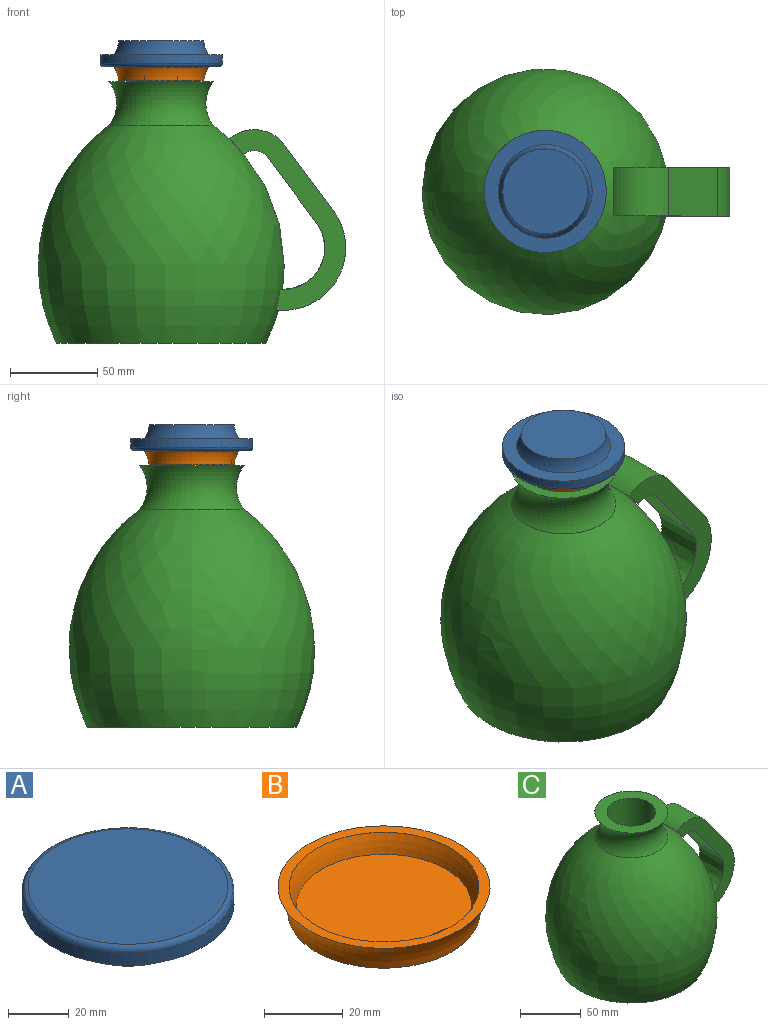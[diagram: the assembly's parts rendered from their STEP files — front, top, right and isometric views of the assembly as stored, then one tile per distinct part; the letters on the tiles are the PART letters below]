
ASSEMBLY  parts=3 mates=2
PART A: 6 faces, bbox 75.8x75.8x17 mm
  f0: plane 48.64x48.64mm, normal (0,0,-1), area 1858.2mm2, adj f1
  f1: torus R=44.22mm, axis (0,0,-1), area 1347.6mm2, adj f0,f2
  f2: plane 70x70mm, normal (0,0,-1), area 1575.2mm2, adj f1,f3
  f3: cylinder r=35mm len=70mm, axis (0,0,-1), area 1099.6mm2, adj f2,f5
  f4: plane 66x66mm, normal (0,0,1), area 3421.2mm2, adj f5
  f5: torus R=33mm, axis (0,0,1), area 676.5mm2, adj f3,f4
PART B: 7 faces, bbox 65.2x65.2x16 mm
  f0: cylinder r=12mm len=18.8mm, axis (0,0,-1), area 69.7mm2, adj f1,f3,f4,f5,f6
  f1: plane 48.84x46.96mm, normal (0,0,-1), area 1790.3mm2, adj f0,f2
  f2: torus R=44.32mm, axis (0,0,-1), area 1353mm2, adj f1,f3,f4
  f3: plane 54x54mm, normal (0,0,1), area 450.8mm2, adj f0,f2,f4,f6
  f4: cylinder r=24.42mm len=18.8mm, axis (0,0,-1), area 154.4mm2, adj f0,f2,f3
  f5: plane 44.55x43.14mm, normal (0,0,1), area 1513.5mm2, adj f0,f6
  f6: torus R=44.32mm, axis (0,0,-1), area 745.5mm2, adj f0,f3,f5
PART C: 16 faces, bbox 176.4x141.1x151.8 mm
  f0: plane 120x120mm, normal (0,0,-1), area 11309.7mm2, adj f1
  f1: revolved ~140.99x140.99mm, area 52192.3mm2, adj f0,f2,f4,f8,f10,f11,f12,f13
  f2: torus R=45.61mm, axis (0,0,-1), area 4597.9mm2, adj f1,f3
  f3: plane 60x60mm, normal (0,0,1), area 1570.8mm2, adj f2,f14
  f4: plane 28x9.21mm, normal (-0.77,0,-0.64), area 210.6mm2, adj f1,f8,f9,f12,f13
  f5: cylinder r=35.77mm len=57.07mm, axis (0,-1,0), area 2280.5mm2, adj f7,f11,f12,f13
  f6: plane 37.75x28mm, normal (-0.8,0,-0.6), area 1316mm2, adj f8,f10,f12,f13
  f7: plane 37.75x28mm, normal (0.8,0,0.6), area 1316mm2, adj f5,f9,f12,f13
  f8: cylinder r=9.77mm len=28mm, axis (0,-1,0), area 445.6mm2, adj f1,f4,f6,f12,f13
  f9: cylinder r=21.77mm len=31.45mm, axis (0,-1,0), area 993mm2, adj f4,f7,f12,f13
  f10: bspline ~37.92x28mm, area 1495.2mm2, adj f1,f6,f12,f13
  f11: plane 28x1.87mm, normal (0,0,-1), area 24.6mm2, adj f1,f5,f12,f13
  f12: plane 103.72x66.57mm, normal (0,-1,0), area 1696.9mm2, adj f1,f4,f5,f6,f7,f8,f9,f10
  f13: plane 103.72x66.57mm, normal (0,1,0), area 1696.6mm2, adj f1,f4,f5,f6,f7,f8,f9,f10
  f14: cylinder r=20mm len=50mm, axis (0,0,1), area 6283.2mm2, adj f3,f15
  f15: plane 40x40mm, normal (0,0,1), area 1256.6mm2, adj f14
PLACE A rot(axis=(1,0,0),180deg) t=(-21.92,6.34,113.82)mm
PLACE B t=(-21.92,6.34,86.69)mm
PLACE C t=(-21.92,6.34,-61.78)mm fixed
MATE slider B.f2 <-> A.f1  axis (0,0,1) through (-21.92,6.34,91.19)mm
MATE slider B.f2 <-> C.f2  axis (0,0,-1) through (-21.92,6.34,88.69)mm
